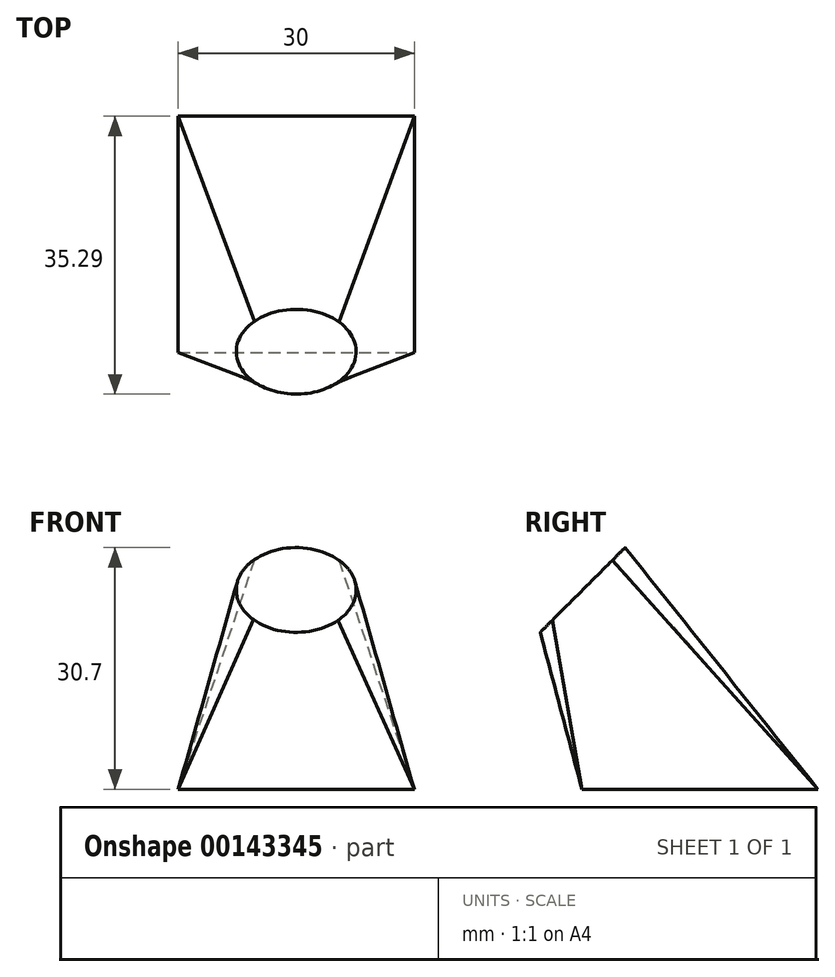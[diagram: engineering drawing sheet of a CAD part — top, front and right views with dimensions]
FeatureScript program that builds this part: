
annotation { "Feature Type Name" : "Feature", "Feature Type Description" : "" }
export const myFeature = defineFeature(function(context is Context, id is Id, definition is map)
    precondition{}
    {
        {
            var Q0;
            Q0=qCreatedBy(makeId("Top.planeOp"),FACE);
            var sketch = newSketch(context, id + "F0", { "sketchPlane" : qUnion([Q0])});
            skLineSegment(sketch, "E0.bottom", {"start": v(-15, 15) * mm, "end": v(15, 15) * mm});
            skLineSegment(sketch, "E0.top", {"start": v(-15, -15) * mm, "end": v(15, -15) * mm});
            skLineSegment(sketch, "E0.left", {"start": v(-15, 15) * mm, "end": v(-15, -15) * mm});
            skLineSegment(sketch, "E0.right", {"start": v(15, 15) * mm, "end": v(15, -15) * mm});
            skPoint(sketch, "E0.middle", {"position": v(0, 0) * mm});
            skSolve(sketch);
        }
        {
            var Q0;
            Q0=qCreatedBy(makeId("Top.planeOp"),FACE);
            cPlane(context, id + "F1", {"entities" : qUnion([Q0]), "cplaneType" : CPlaneType.OFFSET, "offset" : 25 * mm, "width" : 150 * mm, "height" : 150 * mm});
        }
        {
            var Q0;
            Q0=qCreatedBy(id+"F1.planeOp",FACE);
            var sketch = newSketch(context, id + "F2", { "sketchPlane" : qUnion([Q0])});
            skLineSegment(sketch, "E1", {"start": v(0, 0) * mm, "end": v(37.32, 0) * mm, "construction": true});
            skSolve(sketch);
        }
        {
            var Q0;
            Q0=qCreatedBy(makeId("Front.planeOp"),FACE);
            cPlane(context, id + "F3", {"entities" : qUnion([Q0]), "cplaneType" : CPlaneType.OFFSET, "offset" : 15 * mm, "width" : 150 * mm, "height" : 150 * mm});
        }
        {
            var Q0;
            Q0=qCreatedBy(id+"F3.planeOp",FACE);
            var sketch = newSketch(context, id + "F4", { "sketchPlane" : qUnion([Q0])});
            skLineSegment(sketch, "E2", {"start": v(0, 25.22) * mm, "end": v(-24.95, 25.22) * mm, "construction": true});
            skSolve(sketch);
        }
        {
            var Q0;
            Q0=sQuery(id+"F4.wireOp",EDGE,"E2");
            cPlane(context, id + "F5", {"entities" : qUnion([Q0]), "cplaneType" : CPlaneType.LINE_ANGLE, "offset" : 25 * mm, "angle" : 45 * degree, "width" : 150 * mm, "height" : 150 * mm});
        }
        {
            var Q0;
            Q0=qCreatedBy(id+"F5.planeOp",FACE);
            var sketch = newSketch(context, id + "F6", { "sketchPlane" : qUnion([Q0])});
            skCircle(sketch, "E3", {"center": v(0, 7.36) * mm, "radius": 7.61 * mm});
            skPoint(sketch, "E4", {"position": v(-5, 13.1) * mm});
            skPoint(sketch, "E5", {"position": v(5.44, 12.68) * mm});
            skPoint(sketch, "E6", {"position": v(-5.29, 1.88) * mm});
            skPoint(sketch, "E7", {"position": v(5.12, 1.72) * mm});
            skSolve(sketch);
        }
        {
            var Q0;
            Q0=makeQuery(id+"F6.imprint","IMPRINT",FACE,{"disambiguationData":[TD([[makeQuery(id+"F6.imprint","IMPRINT",EDGE,{"derivedFrom":sQuery(id+"F6.wireOp",EDGE,"E3")}),1.0]])]});
            var Q1;
            Q1=makeQuery(id+"F0.imprint","IMPRINT",FACE,{"disambiguationData":[TD([[makeQuery(id+"F0.imprint","IMPRINT",EDGE,{"derivedFrom":sQuery(id+"F0.wireOp",EDGE,"E0.bottom")}),-1.0]])]});
            var Q2;
            Q2=sQuery(id+"F6.wireOp",VERTEX,"E5");
            var Q3;
            Q3=sQuery(id+"F0.wireOp",VERTEX,"E0.right.start");
            loft(context, id + "F7", {"sheetProfilesArray" : [{ "sheetProfileEntities" : qUnion([Q0]) }, { "sheetProfileEntities" : qUnion([Q1]) }], "matchConnections" : true, "connections" : [{ "connectionEntities" : qUnion([Q2, Q3]), "connectionEdgeQueries" : qUnion([]), "connectionEdgeParameters" : [] }]});
        }
    });
